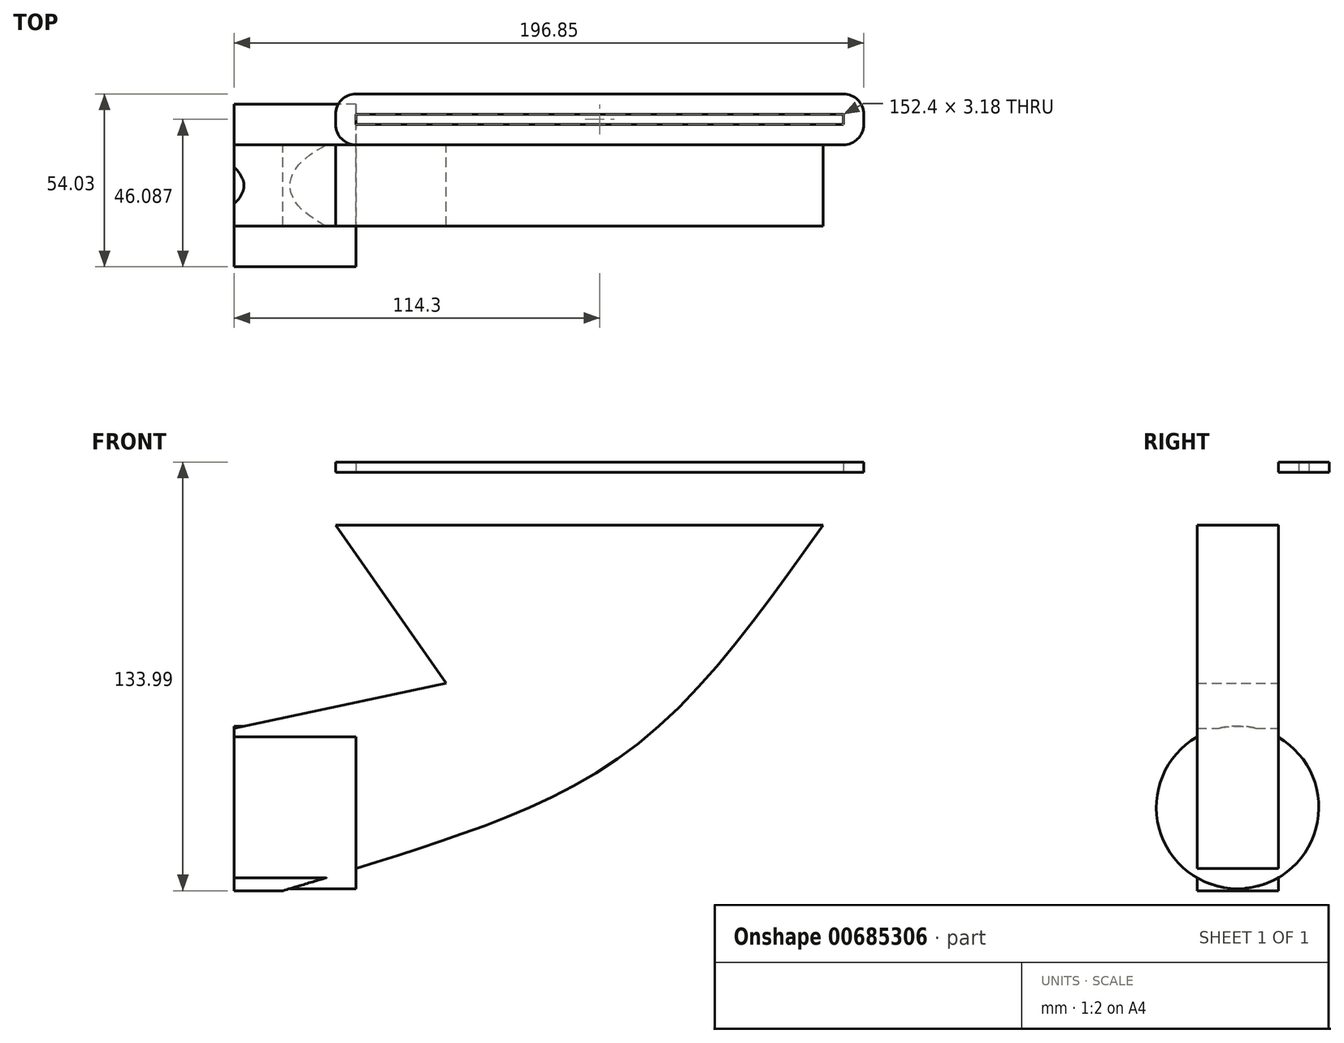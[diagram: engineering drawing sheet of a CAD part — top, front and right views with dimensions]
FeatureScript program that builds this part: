
annotation { "Feature Type Name" : "Feature", "Feature Type Description" : "" }
export const myFeature = defineFeature(function(context is Context, id is Id, definition is map)
    precondition{}
    {
        {
            var Q0;
            Q0=qCreatedBy(makeId("Top.planeOp"),FACE);
            var sketch = newSketch(context, id + "F0", { "sketchPlane" : qUnion([Q0])});
            skLineSegment(sketch, "E0.bottom", {"start": v(6.35, 0) * mm, "end": v(158.75, 0) * mm});
            skLineSegment(sketch, "E0.top", {"start": v(6.35, 15.88) * mm, "end": v(158.75, 15.88) * mm});
            skLineSegment(sketch, "E0.left", {"start": v(0, 6.35) * mm, "end": v(0, 9.53) * mm});
            skLineSegment(sketch, "E0.right", {"start": v(165.1, 6.35) * mm, "end": v(165.1, 9.52) * mm});
            skPoint(sketch, "E1.visualSharp", {"position": v(0, 15.88) * mm});
            skArc(sketch, "E1.filletArc", {"start": v(6.35, 15.88) * mm, "mid": v(1.86, 14.02) * mm, "end": v(0, 9.52) * mm});
            skPoint(sketch, "E2.visualSharp", {"position": v(0, 0) * mm});
            skArc(sketch, "E2.filletArc", {"start": v(0, 6.35) * mm, "mid": v(1.86, 1.86) * mm, "end": v(6.35, 0) * mm});
            skPoint(sketch, "E3.visualSharp", {"position": v(165.1, 15.88) * mm});
            skArc(sketch, "E3.filletArc", {"start": v(165.1, 9.52) * mm, "mid": v(163.24, 14.02) * mm, "end": v(158.75, 15.88) * mm});
            skPoint(sketch, "E4.visualSharp", {"position": v(165.1, 0) * mm});
            skArc(sketch, "E4.filletArc", {"start": v(158.75, 0) * mm, "mid": v(163.24, 1.86) * mm, "end": v(165.1, 6.35) * mm});
            skLineSegment(sketch, "E5.bottom", {"start": v(158.75, 6.35) * mm, "end": v(6.35, 6.35) * mm});
            skLineSegment(sketch, "E5.top", {"start": v(158.75, 9.52) * mm, "end": v(6.35, 9.52) * mm});
            skLineSegment(sketch, "E5.left", {"start": v(158.75, 6.35) * mm, "end": v(158.75, 9.52) * mm});
            skLineSegment(sketch, "E5.right", {"start": v(6.35, 6.35) * mm, "end": v(6.35, 9.52) * mm});
            skSolve(sketch);
        }
        {
            var Q0;
            Q0 = qSketchRegion(id + "F0", true);
            extrude(context, id + "F1", {"entities" : qUnion([Q0]), "depth" : 3.17 * mm, "offsetDistance" : 25.4 * mm});
        }
        {
            var Q0;
            Q0=qCreatedBy(makeId("Front.planeOp"),FACE);
            var sketch = newSketch(context, id + "F2", { "sketchPlane" : qUnion([Q0])});
            skLineSegment(sketch, "E6", {"start": v(0, -16.52) * mm, "end": v(152.4, -16.52) * mm});
            skLineSegment(sketch, "E7", {"start": v(152.4, -16.52) * mm, "end": v(152.4, -130.82) * mm});
            skLineSegment(sketch, "E8", {"start": v(152.4, -130.82) * mm, "end": v(-31.75, -130.82) * mm});
            skLineSegment(sketch, "E9", {"start": v(-31.75, -130.82) * mm, "end": v(-31.75, -80.02) * mm});
            skLineSegment(sketch, "E10", {"start": v(-31.75, -80.02) * mm, "end": v(34.59, -65.98) * mm});
            skLineSegment(sketch, "E11", {"start": v(34.59, -65.98) * mm, "end": v(0, -16.52) * mm});
            skFitSpline(sketch, "E12", {"points": [v(152.4, -16.52) * mm, v(93.94, -85.36) * mm, v(33.8, -115.04) * mm, v(-16.45, -130.82) * mm], "startDerivative": vector(-144.17, -203.85) * mm, "endDerivative": vector(-168.41, -50.42) * mm});
            skSolve(sketch);
        }
        {
            var Q0;
            Q0=makeQuery(id+"F2.imprint","IMPRINT",FACE,{"disambiguationData":[TD([[makeQuery(id+"F2.imprint","IMPRINT",EDGE,{"derivedFrom":sQuery(id+"F2.wireOp",EDGE,"E6")}),-1.0]])]});
            extrude(context, id + "F3", {"entities" : qUnion([Q0]), "depth" : 25.4 * mm, "offsetDistance" : 25.4 * mm});
        }
        {
            var Q0;
            Q0=makeQuery(id+"F3.opExtrude","SWEPT_FACE",FACE,{"disambiguationData":[OSD([sQuery(id+"F2.wireOp",EDGE,"E9")])]});
            var sketch = newSketch(context, id + "F4", { "sketchPlane" : qUnion([Q0])});
            skCircle(sketch, "E13", {"center": v(12.75, -104.77) * mm, "radius": 25.4 * mm});
            skSolve(sketch);
        }
        {
            var Q0;
            Q0 = qSketchRegion(id + "F4", true);
            extrude(context, id + "F5", {"entities" : qUnion([Q0]), "operationType" : NewBodyOperationType.ADD, "oppositeDirection" : true, "depth" : 38.1 * mm, "offsetDistance" : 25.4 * mm});
        }
    });
